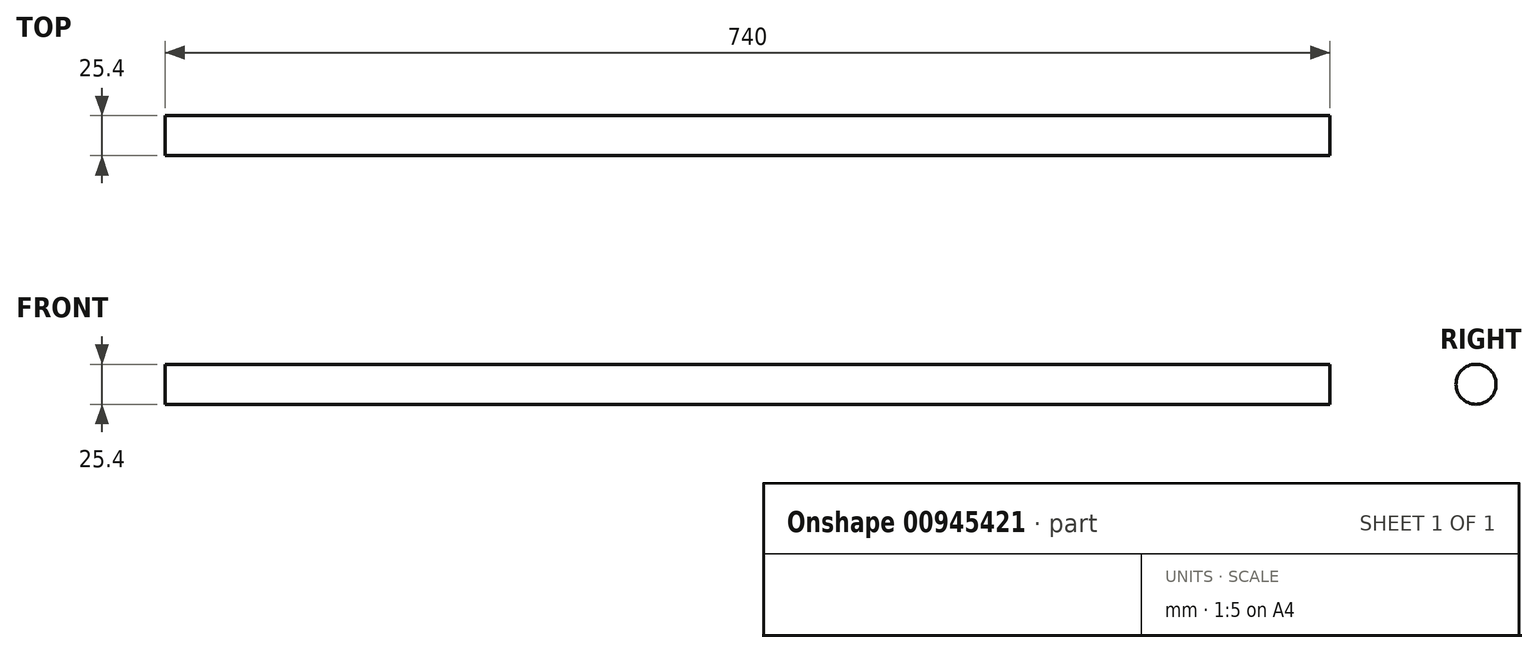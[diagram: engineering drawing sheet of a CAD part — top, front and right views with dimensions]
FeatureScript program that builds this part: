
annotation { "Feature Type Name" : "Feature", "Feature Type Description" : "" }
export const myFeature = defineFeature(function(context is Context, id is Id, definition is map)
    precondition{}
    {
        {
            var Q0;
            Q0=qCreatedBy(makeId("Right.planeOp"),FACE);
            var sketch = newSketch(context, id + "F0", { "sketchPlane" : qUnion([Q0])});
            skCircle(sketch, "E0", {"center": v(0, 0) * mm, "radius": 12.7 * mm});
            skSolve(sketch);
        }
        {
            var Q0;
            Q0=sQuery(id+"F0.wireOp",EDGE,"E0");
            extrude(context, id + "F1", {"bodyType" : ToolBodyType.SURFACE, "surfaceEntities" : qUnion([Q0]), "depth" : 740 * mm, "offsetDistance" : 25.4 * mm});
        }
    });
